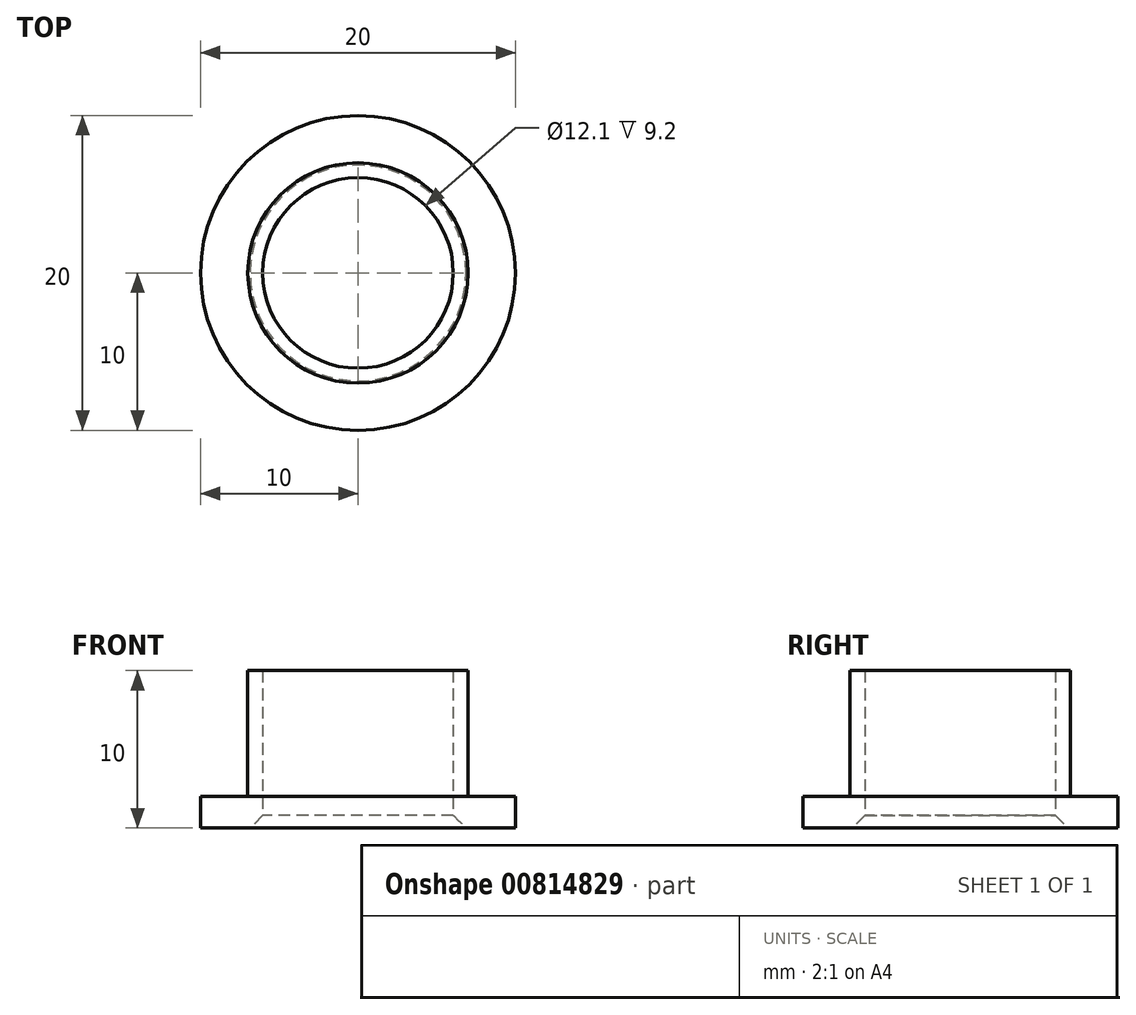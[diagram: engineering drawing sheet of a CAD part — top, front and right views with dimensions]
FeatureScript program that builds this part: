
annotation { "Feature Type Name" : "Feature", "Feature Type Description" : "" }
export const myFeature = defineFeature(function(context is Context, id is Id, definition is map)
    precondition{}
    {
        {
            assignVariable(context, id + "F0", {"name" : "Length", "anyValue" : 10});
        }
        {
            var Q0;
            Q0=qCreatedBy(makeId("Top.planeOp"),FACE);
            var sketch = newSketch(context, id + "F1", { "sketchPlane" : qUnion([Q0])});
            skCircle(sketch, "E0", {"center": v(0, 0) * mm, "radius": 6.05 * mm});
            skCircle(sketch, "E1", {"center": v(0, 0) * mm, "radius": 7 * mm});
            skCircle(sketch, "E2", {"center": v(0, 0) * mm, "radius": 10 * mm});
            skSolve(sketch);
        }
        {
            var Q0;
            Q0=makeQuery(id+"F1.imprint","IMPRINT",FACE,{"disambiguationData":[TD([[makeQuery(id+"F1.imprint","IMPRINT",EDGE,{"derivedFrom":sQuery(id+"F1.wireOp",EDGE,"E1")}),-1.0]])]});
            extrude(context, id + "F2", {"entities" : qUnion([Q0]), "depth" : 2 * mm, "offsetDistance" : 25 * mm});
        }
        {
            var Q0;
            Q0=makeQuery(id+"F1.imprint","IMPRINT",FACE,{"disambiguationData":[TD([[makeQuery(id+"F1.imprint","IMPRINT",EDGE,{"derivedFrom":sQuery(id+"F1.wireOp",EDGE,"E0")}),-1.0]])]});
            extrude(context, id + "F3", {"entities" : qUnion([Q0]), "operationType" : NewBodyOperationType.ADD, "depth" : (getVariable(context, 'Length')) * mm, "offsetDistance" : 25 * mm});
        }
        {
            var Q0;
            Q0=makeQuery(id+"F3.opExtrude","CAP_EDGE",EDGE,{"disambiguationData":[OSD([sQuery(id+"F1.wireOp",EDGE,"E0")])],"isStart":true});
            chamfer(context, id + "F4", {"entities" : qUnion([Q0]), "width" : 0.8 * mm, "tangentPropagation" : true});
        }
    });
